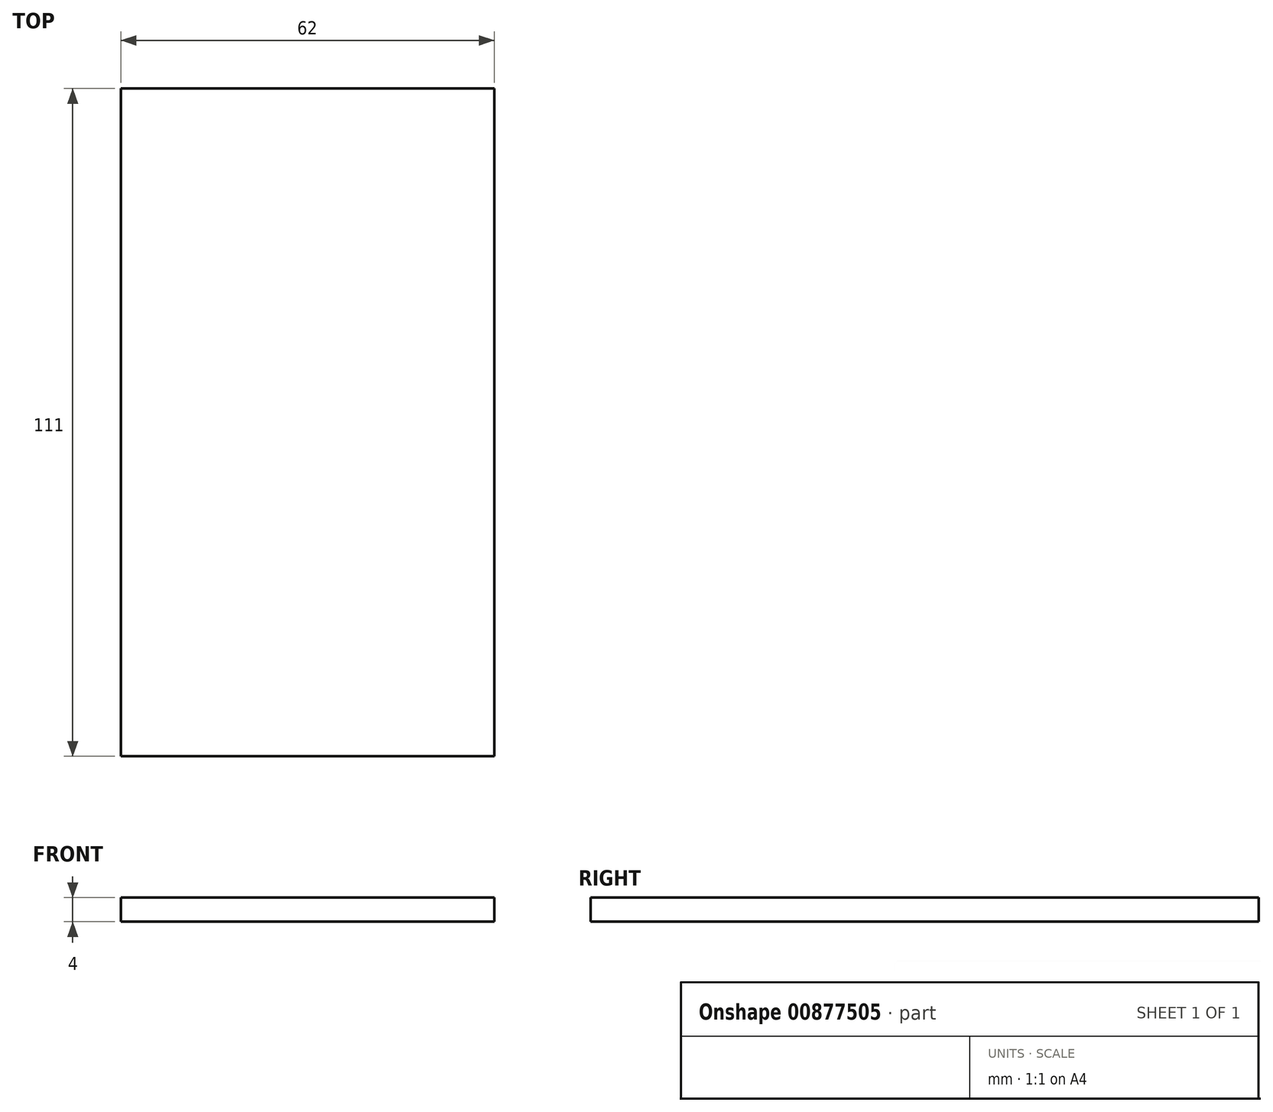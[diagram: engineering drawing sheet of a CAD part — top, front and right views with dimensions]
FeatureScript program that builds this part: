
annotation { "Feature Type Name" : "Feature", "Feature Type Description" : "" }
export const myFeature = defineFeature(function(context is Context, id is Id, definition is map)
    precondition{}
    {
        {
            var Q0;
            Q0=qCreatedBy(makeId("Top.planeOp"),FACE);
            var sketch = newSketch(context, id + "F0", { "sketchPlane" : qUnion([Q0])});
            skLineSegment(sketch, "E0.bottom", {"start": v(31, -55.5) * mm, "end": v(-31, -55.5) * mm});
            skLineSegment(sketch, "E0.top", {"start": v(31, 55.5) * mm, "end": v(-31, 55.5) * mm});
            skLineSegment(sketch, "E0.left", {"start": v(31, -55.5) * mm, "end": v(31, 55.5) * mm});
            skLineSegment(sketch, "E0.right", {"start": v(-31, -55.5) * mm, "end": v(-31, 55.5) * mm});
            skPoint(sketch, "E0.middle", {"position": v(0, 0) * mm});
            skSolve(sketch);
        }
        {
            var Q0;
            Q0=makeQuery(id+"F0.imprint","IMPRINT",FACE,{"disambiguationData":[TD([[makeQuery(id+"F0.imprint","IMPRINT",EDGE,{"derivedFrom":sQuery(id+"F0.wireOp",EDGE,"E0.bottom")}),-1.0]])]});
            extrude(context, id + "F1", {"entities" : qUnion([Q0]), "depth" : 4 * mm, "offsetDistance" : 25.4 * mm});
        }
    });
